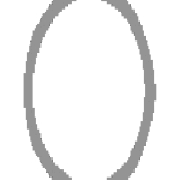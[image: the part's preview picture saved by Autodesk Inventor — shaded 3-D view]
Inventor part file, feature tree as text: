
AUTODESK INVENTOR PART (.ipt)
format: ipt  version: 2021 (Build 250183000, 183)  size: 144,384 bytes
history: native  units: in
note: dims shown in document units (in); Inventor stores cm internally (conversion verified against a paired STEP export)
features: other x5, sketch x2, sweep x1, plane x1
ambient origin geometry x8: Origin, YZ Plane, XZ Plane, XY Plane, X Axis, Y Axis, Z Axis, Center Point
bodies: Solid1 (feature_tree), Body (feature_tree)
feature tree (9):
  other  "Driven Length"
  other  "Frame Generator"
  other  "Start Plane"
  other  "End Plane"
  sweep  "Sweep Path"
  other  "Orientation Work Plane"
  sketch  "Sketch2"  dims[d0=1.0in d1=0.065in]
  plane  "Work Plane3"
  sketch  "Sketch3"  dims[d2=1.1738in d4=-0.0in d5=1.1738in d8=90.0deg d9=1.1738in d10=0.0in d11=0.0in]
